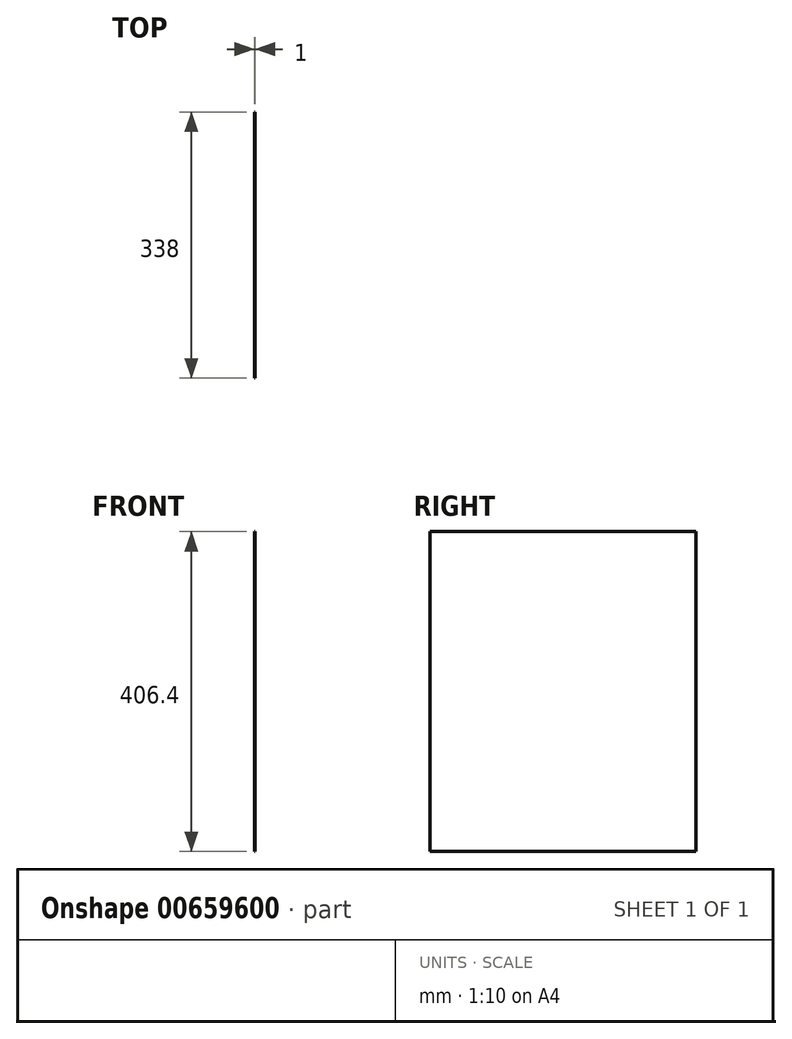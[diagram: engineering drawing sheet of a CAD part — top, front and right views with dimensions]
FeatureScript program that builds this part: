
annotation { "Feature Type Name" : "Feature", "Feature Type Description" : "" }
export const myFeature = defineFeature(function(context is Context, id is Id, definition is map)
    precondition{}
    {
        {
            var Q0;
            Q0=qCreatedBy(makeId("Right.planeOp"),FACE);
            var sketch = newSketch(context, id + "F0", { "sketchPlane" : qUnion([Q0])});
            skLineSegment(sketch, "E0.bottom", {"start": v(169, -203.2) * mm, "end": v(-169, -203.2) * mm});
            skLineSegment(sketch, "E0.top", {"start": v(169, 203.2) * mm, "end": v(-169, 203.2) * mm});
            skLineSegment(sketch, "E0.left", {"start": v(169, -203.2) * mm, "end": v(169, 203.2) * mm});
            skLineSegment(sketch, "E0.right", {"start": v(-169, -203.2) * mm, "end": v(-169, 203.2) * mm});
            skPoint(sketch, "E0.middle", {"position": v(0, 0) * mm});
            skSolve(sketch);
        }
        {
            var Q0;
            Q0=qSketchRegion(id+"F0",true);
            extrude(context, id + "F1", {"entities" : qUnion([Q0]), "depth" : 1 * mm, "offsetDistance" : 25 * mm});
        }
    });
